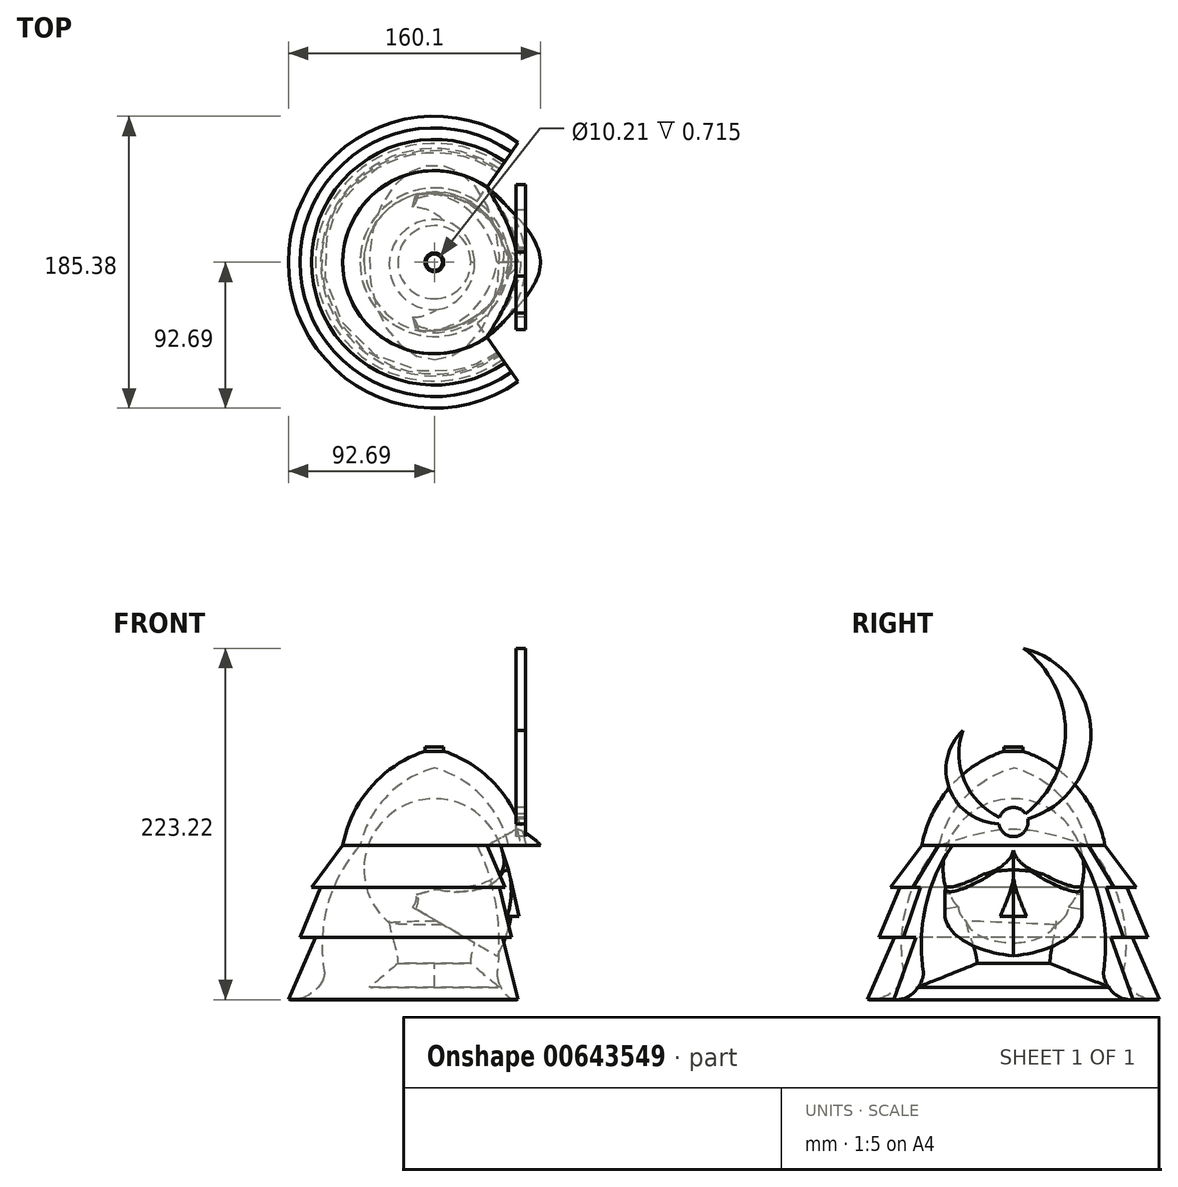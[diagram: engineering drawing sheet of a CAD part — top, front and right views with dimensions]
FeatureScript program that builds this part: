
annotation { "Feature Type Name" : "Feature", "Feature Type Description" : "" }
export const myFeature = defineFeature(function(context is Context, id is Id, definition is map)
    precondition{}
    {
        {
            var Q0;
            Q0=qCreatedBy(makeId("Top.planeOp"),FACE);
            var sketch = newSketch(context, id + "F0", { "sketchPlane" : qUnion([Q0])});
            skArc(sketch, "E0", {"start": v(-44.68, 0) * mm, "mid": v(0, -44.68) * mm, "end": v(44.68, 0) * mm});
            skLineSegment(sketch, "E1", {"start": v(44.68, 0) * mm, "end": v(-44.68, 0) * mm});
            skLineSegment(sketch, "E2", {"start": v(44.68, 0) * mm, "end": v(44.68, 36.03) * mm, "construction": true});
            skSolve(sketch);
        }
        {
            var Q0;
            Q0=qSketchRegion(id+"F0",true);
            var Q1;
            Q1=sQuery(id+"F0.wireOp",EDGE,"E1");
            revolve(context, id + "F1", {"entities" : qUnion([Q0]), "axis" : qUnion([Q1]), "revolveType" : RevolveType.FULL});
        }
        {
            var Q0;
            Q0=makeQuery(id+"F1.opRevolve","SWEPT_BODY",BODY,{"disambiguationData":[OSD([sQuery(id+"F0.wireOp",EDGE,"E0"),sQuery(id+"F0.wireOp",EDGE,"E1")])]});
            var Q1;
            Q1=qCreatedBy(makeId("Top.planeOp"),FACE);
            transform(context, id + "F2", {"entities" : qUnion([Q0]), "transformType" : TransformType.TRANSLATION_DISTANCE, "transformDirection" : qUnion([Q1]), "distance" : 15 * mm, "oppositeDirection" : true, "makeCopy" : false});
        }
        {
            var Q0;
            Q0=qCreatedBy(makeId("Top.planeOp"),FACE);
            var sketch = newSketch(context, id + "F3", { "sketchPlane" : qUnion([Q0])});
            skLineSegment(sketch, "E3", {"start": v(0, 0) * mm, "end": v(12.34, -43.08) * mm});
            skArc(sketch, "E4", {"start": v(12.34, -43.08) * mm, "mid": v(50.67, -33.3) * mm, "end": v(72.02, 0) * mm});
            skLineSegment(sketch, "E5.MirrorCS", {"start": v(0, 0) * mm, "end": v(12.34, 43.08) * mm});
            skLineSegment(sketch, "E6.MirrorCS", {"start": v(12.34, 43.08) * mm, "end": v(12.34, 43.08) * mm});
            skArc(sketch, "E7.MirrorCS", {"start": v(12.34, 43.08) * mm, "mid": v(50.67, 33.3) * mm, "end": v(72.02, 0) * mm});
            skLineSegment(sketch, "E8", {"start": v(0, -61.4) * mm, "end": v(0, 61.38) * mm, "construction": true});
            skPoint(sketch, "E9", {"position": v(42.07, 0) * mm});
            skSolve(sketch);
        }
        {
            var Q0;
            Q0=qSketchRegion(id+"F3",true);
            var Q1;
            Q1=sQuery(id+"F3.wireOp",EDGE,"E8");
            revolve(context, id + "F4", {"entities" : qUnion([Q0]), "axis" : qUnion([Q1]), "revolveType" : RevolveType.ONE_DIRECTION, "angle" : 45 * degree});
        }
        {
            var Q0;
            Q0=makeQuery(id+"F4.opRevolve","SWEPT_BODY",BODY,{"disambiguationData":[OSD([sQuery(id+"F3.wireOp",EDGE,"E3"),sQuery(id+"F3.wireOp",EDGE,"17598f5f-404b-4f8c-ac35-278ca7a2c35a"),sQuery(id+"F3.wireOp",EDGE,"E4"),sQuery(id+"F3.wireOp",EDGE,"5336d24a-33b8-4873-b715-2a8792ee797a"),sQuery(id+"F3.wireOp",EDGE,"E5.MirrorCS"),sQuery(id+"F3.wireOp",EDGE,"E6.MirrorCS"),sQuery(id+"F3.wireOp",EDGE,"E7.MirrorCS"),sQuery(id+"F3.wireOp",EDGE,"d338a3b0-5d36-45a3-872c-7f8dcec3f61b0.MirrorCS")])]});
            var Q1;
            Q1=sQuery(id+"F3.wireOp",EDGE,"E8");
            var Q2;
            Q2=qCreatedBy(makeId("Top.planeOp"),FACE);
            transform(context, id + "F5", {"entities" : qUnion([Q0]), "transformType" : TransformType.TRANSLATION_DISTANCE, "transformDirection" : qUnion([Q2]), "distance" : 15.56 * mm, "oppositeDirection" : true, "makeCopy" : false});
        }
        {
            var Q0;
            Q0=makeQuery(id+"F4.opRevolve","SWEPT_BODY",BODY,{"disambiguationData":[OSD([sQuery(id+"F3.wireOp",EDGE,"E3"),sQuery(id+"F3.wireOp",EDGE,"17598f5f-404b-4f8c-ac35-278ca7a2c35a"),sQuery(id+"F3.wireOp",EDGE,"E4"),sQuery(id+"F3.wireOp",EDGE,"5336d24a-33b8-4873-b715-2a8792ee797a"),sQuery(id+"F3.wireOp",EDGE,"E5.MirrorCS"),sQuery(id+"F3.wireOp",EDGE,"E6.MirrorCS"),sQuery(id+"F3.wireOp",EDGE,"E7.MirrorCS"),sQuery(id+"F3.wireOp",EDGE,"d338a3b0-5d36-45a3-872c-7f8dcec3f61b0.MirrorCS")])]});
            var Q1;
            Q1=qCreatedBy(makeId("Right.planeOp"),FACE);
            transform(context, id + "F6", {"entities" : qUnion([Q0]), "transformType" : TransformType.TRANSLATION_DISTANCE, "transformDirection" : qUnion([Q1]), "distance" : 29.06 * mm, "oppositeDirection" : true, "makeCopy" : false});
        }
        {
            var Q0;
            Q0=makeQuery(id+"F4.opRevolve","SWEPT_BODY",BODY,{"disambiguationData":[OSD([sQuery(id+"F3.wireOp",EDGE,"E3"),sQuery(id+"F3.wireOp",EDGE,"E4"),sQuery(id+"F3.wireOp",EDGE,"E5.MirrorCS"),sQuery(id+"F3.wireOp",EDGE,"E7.MirrorCS")])]});
            var Q1;
            Q1=sQuery(id+"F0.wireOp",EDGE,"E2");
            transform(context, id + "F7", {"entities" : qUnion([Q0]), "transformType" : TransformType.ROTATION, "transformAxis" : qUnion([Q1]), "angle" : 15 * degree, "oppositeDirection" : true, "makeCopy" : false});
        }
        {
            var Q0;
            Q0=makeQuery(id+"F1.opRevolve","SWEPT_BODY",BODY,{"disambiguationData":[OSD([sQuery(id+"F0.wireOp",EDGE,"E0"),sQuery(id+"F0.wireOp",EDGE,"E1")])]});
            var Q1;
            Q1=makeQuery(id+"F4.opRevolve","SWEPT_BODY",BODY,{"disambiguationData":[OSD([sQuery(id+"F3.wireOp",EDGE,"E3"),sQuery(id+"F3.wireOp",EDGE,"17598f5f-404b-4f8c-ac35-278ca7a2c35a"),sQuery(id+"F3.wireOp",EDGE,"E4"),sQuery(id+"F3.wireOp",EDGE,"5336d24a-33b8-4873-b715-2a8792ee797a"),sQuery(id+"F3.wireOp",EDGE,"E5.MirrorCS"),sQuery(id+"F3.wireOp",EDGE,"E6.MirrorCS"),sQuery(id+"F3.wireOp",EDGE,"E7.MirrorCS"),sQuery(id+"F3.wireOp",EDGE,"d338a3b0-5d36-45a3-872c-7f8dcec3f61b0.MirrorCS")])]});
            booleanBodies(context, id + "F8", {"operationType" : BooleanOperationType.UNION, "tools" : qUnion([Q0, Q1])});
        }
        {
            var Q0;
            Q0=qCreatedBy(makeId("Front.planeOp"),FACE);
            var sketch = newSketch(context, id + "F9", { "sketchPlane" : qUnion([Q0])});
            skLineSegment(sketch, "E10", {"start": v(-75.5, -58.39) * mm, "end": v(-92.69, -97.86) * mm});
            skLineSegment(sketch, "E11", {"start": v(0, 63.89) * mm, "end": v(0, -69.8) * mm, "construction": true});
            skLineSegment(sketch, "E12", {"start": v(-72.2, -26.73) * mm, "end": v(-85.33, -58.39) * mm});
            skLineSegment(sketch, "E13", {"start": v(-85.33, -58.39) * mm, "end": v(-75.5, -58.39) * mm});
            skLineSegment(sketch, "E14", {"start": v(-58.16, 0) * mm, "end": v(-78.04, -26.73) * mm});
            skLineSegment(sketch, "E15", {"start": v(-78.04, -26.73) * mm, "end": v(-72.2, -26.73) * mm});
            skLineSegment(sketch, "E16", {"start": v(-47.17, 0) * mm, "end": v(-58.16, 0) * mm});
            skArc(sketch, "E17", {"start": v(-47.17, 0) * mm, "mid": v(-67.66, -37.09) * mm, "end": v(-69.99, -79.4) * mm});
            skArc(sketch, "E18", {"start": v(-92.69, -97.86) * mm, "mid": v(-79.74, -95.06) * mm, "end": v(-70.78, -85.3) * mm});
            skPoint(sketch, "E19.visualSharp", {"position": v(-69.53, -81.9) * mm});
            skArc(sketch, "E19.filletArc", {"start": v(-70.78, -85.3) * mm, "mid": v(-69.93, -82.4) * mm, "end": v(-69.99, -79.4) * mm});
            skSolve(sketch);
        }
        {
            var Q0;
            {var subQ6=sQuery(id+"F9.wireOp",EDGE,"bed17606-2d73-4af0-a236-4f785531fa8f");Q0=makeQuery(id+"F9.imprint","IMPRINT",FACE,{"disambiguationData":[TD([[makeQuery(id+"F9.imprint","IMPRINT",EDGE,{"derivedFrom":subQ6}),1.0]])]});}
            var Q1;
            {var subQ3=sQuery(id+"F9.wireOp",EDGE,"3992ad86-beb6-407e-abb3-2c1991481c55");Q1=makeQuery(id+"F9.imprint","IMPRINT",FACE,{"disambiguationData":[TD([[makeQuery(id+"F9.imprint","IMPRINT",EDGE,{"derivedFrom":subQ3}),1.0]])]});}
            var Q2;
            {var subQ3=sQuery(id+"F9.wireOp",EDGE,"4294b020-6c44-4885-9173-856c7b450247");Q2=makeQuery(id+"F9.imprint","IMPRINT",FACE,{"disambiguationData":[TD([[makeQuery(id+"F9.imprint","IMPRINT",EDGE,{"derivedFrom":subQ3}),1.0]])]});}
            var Q3;
            {var subQ7=sQuery(id+"F9.wireOp",EDGE,"4294b020-6c44-4885-9173-856c7b450247");Q3=makeQuery(id+"F9.imprint","IMPRINT",FACE,{"disambiguationData":[TD([[makeQuery(id+"F9.imprint","IMPRINT",EDGE,{"derivedFrom":subQ7}),-1.0]])]});}
            var Q4;
            {var subQ2=sQuery(id+"F9.wireOp",EDGE,"3992ad86-beb6-407e-abb3-2c1991481c55");Q4=makeQuery(id+"F9.imprint","IMPRINT",FACE,{"disambiguationData":[TD([[makeQuery(id+"F9.imprint","IMPRINT",EDGE,{"derivedFrom":subQ2}),-1.0]])]});}
            var Q5;
            {var subQ0=sQuery(id+"F9.wireOp",EDGE,"E13");var subQ3=sQuery(id+"F9.wireOp",EDGE,"E12");var subQ4=makeQuery(id+"F9.imprint","INTERSECT",VERTEX,{"derivedFrom":[subQ3,subQ0]});Q5=makeQuery(id+"F9.imprint","IMPRINT",FACE,{"disambiguationData":[TD([[makeQuery(id+"F9.imprint","IMPRINT",EDGE,{"disambiguationData":[TD([[subQ4,-1.0]])],"derivedFrom":subQ0}),1.0]])]});}
            var Q6;
            {var subQ0=sQuery(id+"F9.wireOp",EDGE,"E15");var subQ3=sQuery(id+"F9.wireOp",EDGE,"E14");var subQ4=makeQuery(id+"F9.imprint","INTERSECT",VERTEX,{"derivedFrom":[subQ3,subQ0]});Q6=makeQuery(id+"F9.imprint","IMPRINT",FACE,{"disambiguationData":[TD([[makeQuery(id+"F9.imprint","IMPRINT",EDGE,{"disambiguationData":[TD([[subQ4,-1.0]])],"derivedFrom":subQ0}),1.0]])]});}
            var Q7;
            Q7=sQuery(id+"F9.wireOp",EDGE,"E11");
            revolve(context, id + "F10", {"entities" : qUnion([Q0, Q1, Q2, Q3, Q4, Q5, Q6]), "axis" : qUnion([Q7]), "revolveType" : RevolveType.SYMMETRIC, "angle" : 250 * degree});
        }
        {
            var Q0;
            Q0=qCreatedBy(makeId("Right.planeOp"),FACE);
            var sketch = newSketch(context, id + "F11", { "sketchPlane" : qUnion([Q0])});
            skArc(sketch, "E20", {"start": v(0, 61.56) * mm, "mid": v(-38.19, 39.4) * mm, "end": v(-58.14, 0) * mm});
            skArc(sketch, "E21", {"start": v(0, 49.28) * mm, "mid": v(-30.36, 31.11) * mm, "end": v(-47.2, 0) * mm});
            skLineSegment(sketch, "E22", {"start": v(0, 61.56) * mm, "end": v(0, 49.28) * mm});
            skLineSegment(sketch, "E23", {"start": v(-58.14, 0) * mm, "end": v(-47.2, 0) * mm});
            skSolve(sketch);
        }
        {
            var Q0;
            Q0=makeQuery(id+"F11.imprint","IMPRINT",FACE,{"disambiguationData":[TD([[makeQuery(id+"F11.imprint","IMPRINT",EDGE,{"derivedFrom":sQuery(id+"F11.wireOp",EDGE,"E20")}),1.0]])]});
            var Q1;
            Q1=sQuery(id+"F11.wireOp",EDGE,"E22");
            revolve(context, id + "F12", {"entities" : qUnion([Q0]), "axis" : qUnion([Q1]), "revolveType" : RevolveType.FULL});
        }
        {
            var Q0;
            Q0=qCreatedBy(makeId("Right.planeOp"),FACE);
            var sketch = newSketch(context, id + "F13", { "sketchPlane" : qUnion([Q0])});
            skArc(sketch, "E24", {"start": v(-32.22, 58.1) * mm, "mid": v(-38.56, 16.6) * mm, "end": v(0, 0) * mm});
            skArc(sketch, "E25", {"start": v(-32.22, 58.1) * mm, "mid": v(-29.07, 21.86) * mm, "end": v(0, 0) * mm});
            skCircle(sketch, "E26", {"center": v(0, 0) * mm, "radius": 9.26 * mm});
            skArc(sketch, "E27", {"start": v(0, 0) * mm, "mid": v(49.07, 52.54) * mm, "end": v(6.38, 110.39) * mm});
            skArc(sketch, "E28", {"start": v(0, 0) * mm, "mid": v(32.95, 53.47) * mm, "end": v(6.38, 110.39) * mm});
            skSolve(sketch);
        }
        {
            var Q0;
            Q0=qSketchRegion(id+"F13",true);
            extrude(context, id + "F14", {"entities" : qUnion([Q0]), "depth" : 6 * mm});
        }
        {
            var Q0;
            Q0=makeQuery(id+"F14.opExtrude","SWEPT_BODY",BODY,{"disambiguationData":[OSD([sQuery(id+"F13.wireOp",EDGE,"63a4e0e8-54da-4c7c-8e49-798323a95d9c0.MirrorCS"),sQuery(id+"F13.wireOp",EDGE,"63a4e0e8-54da-4c7c-8e49-798323a95d9c1.MirrorCS"),sQuery(id+"F13.wireOp",EDGE,"63a4e0e8-54da-4c7c-8e49-798323a95d9c2.MirrorCS"),sQuery(id+"F13.wireOp",EDGE,"63a4e0e8-54da-4c7c-8e49-798323a95d9c3.MirrorCS"),sQuery(id+"F13.wireOp",EDGE,"63a4e0e8-54da-4c7c-8e49-798323a95d9c4.MirrorCS"),sQuery(id+"F13.wireOp",EDGE,"63a4e0e8-54da-4c7c-8e49-798323a95d9c5.MirrorCS")])]});
            var Q1;
            Q1=makeQuery(id+"F14.opExtrude","SWEPT_BODY",BODY,{"disambiguationData":[OSD([sQuery(id+"F13.wireOp",EDGE,"E24"),sQuery(id+"F13.wireOp",EDGE,"b7e1e591-e3d9-4fc4-9fd9-ac906eb5375b"),sQuery(id+"F13.wireOp",EDGE,"b3045065-7fd3-4527-97a0-abc5098df0ba"),sQuery(id+"F13.wireOp",EDGE,"015c9c46-c47a-4591-99de-78b190910ab0"),sQuery(id+"F13.wireOp",EDGE,"8cbf14fa-2419-4e41-a801-432650f1cecd"),sQuery(id+"F13.wireOp",EDGE,"E25")])]});
            var Q2;
            Q2=qCreatedBy(makeId("Right.planeOp"),FACE);
            transform(context, id + "F15", {"entities" : qUnion([Q0, Q1]), "transformType" : TransformType.TRANSLATION_DISTANCE, "transformDirection" : qUnion([Q2]), "distance" : 51.95 * mm, "makeCopy" : false});
        }
        {
            var Q0;
            Q0=qCreatedBy(makeId("Front.planeOp"),FACE);
            var sketch = newSketch(context, id + "F16", { "sketchPlane" : qUnion([Q0])});
            skLineSegment(sketch, "E29.bottom", {"start": v(0, 62.6) * mm, "end": v(-5.96, 62.6) * mm});
            skLineSegment(sketch, "E29.top", {"start": v(0, 58.52) * mm, "end": v(-5.96, 58.52) * mm});
            skLineSegment(sketch, "E29.left", {"start": v(0, 62.6) * mm, "end": v(0, 58.52) * mm});
            skLineSegment(sketch, "E29.right", {"start": v(-5.96, 62.6) * mm, "end": v(-5.96, 58.52) * mm});
            skLineSegment(sketch, "E30.bottom", {"start": v(-5.1, 62.9) * mm, "end": v(1.24, 62.9) * mm});
            skLineSegment(sketch, "E30.top", {"start": v(-5.1, 61.9) * mm, "end": v(1.24, 61.9) * mm});
            skLineSegment(sketch, "E30.left", {"start": v(-5.1, 62.9) * mm, "end": v(-5.1, 61.9) * mm});
            skLineSegment(sketch, "E30.right", {"start": v(1.24, 62.9) * mm, "end": v(1.24, 61.9) * mm});
            skSolve(sketch);
        }
        {
            var Q0;
            {var subQ8=sQuery(id+"F16.wireOp",EDGE,"E29.top");Q0=makeQuery(id+"F16.imprint","IMPRINT",FACE,{"disambiguationData":[TD([[makeQuery(id+"F16.imprint","IMPRINT",EDGE,{"derivedFrom":subQ8}),-1.0]])]});}
            var Q1;
            Q1=sQuery(id+"F11.wireOp",EDGE,"E22");
            revolve(context, id + "F17", {"operationType" : NewBodyOperationType.ADD, "entities" : qUnion([Q0]), "axis" : qUnion([Q1]), "revolveType" : RevolveType.FULL});
        }
        {
            var Q0;
            Q0=makeQuery(id+"F14.opExtrude","SWEPT_BODY",BODY,{"disambiguationData":[OSD([sQuery(id+"F13.wireOp",EDGE,"E24"),sQuery(id+"F13.wireOp",EDGE,"b7e1e591-e3d9-4fc4-9fd9-ac906eb5375b"),sQuery(id+"F13.wireOp",EDGE,"b3045065-7fd3-4527-97a0-abc5098df0ba"),sQuery(id+"F13.wireOp",EDGE,"015c9c46-c47a-4591-99de-78b190910ab0"),sQuery(id+"F13.wireOp",EDGE,"8cbf14fa-2419-4e41-a801-432650f1cecd"),sQuery(id+"F13.wireOp",EDGE,"E25"),sQuery(id+"F13.wireOp",EDGE,"63a4e0e8-54da-4c7c-8e49-798323a95d9c0.MirrorCS"),sQuery(id+"F13.wireOp",EDGE,"63a4e0e8-54da-4c7c-8e49-798323a95d9c1.MirrorCS"),sQuery(id+"F13.wireOp",EDGE,"63a4e0e8-54da-4c7c-8e49-798323a95d9c2.MirrorCS"),sQuery(id+"F13.wireOp",EDGE,"63a4e0e8-54da-4c7c-8e49-798323a95d9c3.MirrorCS"),sQuery(id+"F13.wireOp",EDGE,"63a4e0e8-54da-4c7c-8e49-798323a95d9c4.MirrorCS"),sQuery(id+"F13.wireOp",EDGE,"63a4e0e8-54da-4c7c-8e49-798323a95d9c5.MirrorCS"),sQuery(id+"F13.wireOp",EDGE,"E26")])]});
            var Q1;
            Q1=qCreatedBy(makeId("Top.planeOp"),FACE);
            transform(context, id + "F18", {"entities" : qUnion([Q0]), "transformType" : TransformType.TRANSLATION_DISTANCE, "transformDirection" : qUnion([Q1]), "distance" : 14.88 * mm, "makeCopy" : false});
        }
        {
            var Q0;
            Q0=qCreatedBy(makeId("Front.planeOp"),FACE);
            var sketch = newSketch(context, id + "F19", { "sketchPlane" : qUnion([Q0])});
            skLineSegment(sketch, "E31", {"start": v(67.4, 0.05) * mm, "end": v(55, 0.05) * mm});
            skLineSegment(sketch, "E32", {"start": v(55, 0.05) * mm, "end": v(52.48, 10.4) * mm});
            skArc(sketch, "E33", {"start": v(67.4, 0.05) * mm, "mid": v(60.62, 6.2) * mm, "end": v(52.48, 10.4) * mm});
            skSolve(sketch);
        }
        {
            var Q0;
            Q0=makeQuery(id+"F10.opRevolve","CAP_VERTEX",VERTEX,{"disambiguationData":[OSD([sQuery(id+"F9.wireOp",EDGE,"E14"),sQuery(id+"F9.wireOp",EDGE,"E16")])],"isStart":true});
            var Q1;
            Q1=makeQuery(id+"F19.imprint","IMPRINT",FACE,{"disambiguationData":[TD([[makeQuery(id+"F19.imprint","IMPRINT",EDGE,{"derivedFrom":sQuery(id+"F19.wireOp",EDGE,"E31")}),-1.0]])]});
            var Q2;
            Q2=makeQuery(id+"F10.opRevolve","CAP_VERTEX",VERTEX,{"disambiguationData":[OSD([sQuery(id+"F9.wireOp",EDGE,"E14"),sQuery(id+"F9.wireOp",EDGE,"E16")])],"isStart":false});
            loft(context, id + "F20", {"sheetProfilesArray" : [{ "sheetProfileEntities" : qUnion([Q0]) }, { "sheetProfileEntities" : qUnion([Q1]) }, { "sheetProfileEntities" : qUnion([Q2]) }]});
        }
        {
            var Q0;
            Q0=qCreatedBy(makeId("Top.planeOp"),FACE);
            cPlane(context, id + "F21", {"entities" : qUnion([Q0]), "cplaneType" : CPlaneType.OFFSET, "offset" : 90 * mm, "oppositeDirection" : true, "width" : 150 * mm, "height" : 150 * mm});
        }
        {
            var Q0;
            Q0=qCreatedBy(id+"F21.planeOp",FACE);
            var sketch = newSketch(context, id + "F22", { "sketchPlane" : qUnion([Q0])});
            skEllipse(sketch, "E34", {"center": v(0, 0) * mm, "majorRadius": 61.75 * mm, "minorRadius": 41.4 * mm, "majorAxis": v(0, -1)});
            skSolve(sketch);
        }
        {
            var Q0;
            Q0=qCreatedBy(id+"F21.planeOp",FACE);
            cPlane(context, id + "F23", {"entities" : qUnion([Q0]), "cplaneType" : CPlaneType.OFFSET, "offset" : 15 * mm, "width" : 150 * mm, "height" : 150 * mm});
        }
        {
            var Q0;
            Q0=qCreatedBy(id+"F23.planeOp",FACE);
            var sketch = newSketch(context, id + "F24", { "sketchPlane" : qUnion([Q0])});
            skCircle(sketch, "E35", {"center": v(0, 0) * mm, "radius": 23.2 * mm});
            skSolve(sketch);
        }
        {
            var Q0;
            Q0=qCreatedBy(id+"F23.planeOp",FACE);
            cPlane(context, id + "F25", {"entities" : qUnion([Q0]), "cplaneType" : CPlaneType.OFFSET, "offset" : 30 * mm, "width" : 150 * mm, "height" : 150 * mm});
        }
        {
            var Q0;
            Q0=qCreatedBy(id+"F25.planeOp",FACE);
            var sketch = newSketch(context, id + "F26", { "sketchPlane" : qUnion([Q0])});
            skCircle(sketch, "E36", {"center": v(0, -1.42) * mm, "radius": 28.98 * mm});
            skArc(sketch, "E37", {"start": v(33.36, -9.72) * mm, "mid": v(45.44, -8.86) * mm, "end": v(53.7, 0) * mm});
            skArc(sketch, "E38.MirrorCS", {"start": v(33.36, 9.72) * mm, "mid": v(45.44, 8.86) * mm, "end": v(53.7, 0) * mm});
            skLineSegment(sketch, "E39", {"start": v(33.36, -9.72) * mm, "end": v(33.36, 9.72) * mm});
            skSolve(sketch);
        }
        {
            var Q1;
            {var subQ0=sQuery(id+"F3.wireOp",EDGE,"E4");var subQ1=sQuery(id+"F3.wireOp",EDGE,"E7.MirrorCS");Q1=makeQuery(id+"F8.opBoolean","SPLIT",FACE,{"disambiguationData":[TD([makeQuery(id+"F1.opRevolve","SWEPT_FACE",FACE,{"disambiguationData":[OSD([sQuery(id+"F0.wireOp",EDGE,"E0")])]}),makeQuery(id+"F4.opRevolve","SWEPT_FACE",FACE,{"disambiguationData":[OSD([subQ0])]}),makeQuery(id+"F4.opRevolve","SWEPT_FACE",FACE,{"disambiguationData":[OSD([subQ1])]})])],"derivedFrom":makeQuery(id+"F4.opRevolve","CAP_FACE",FACE,{"disambiguationData":[OSD([sQuery(id+"F3.wireOp",EDGE,"E3"),subQ0,sQuery(id+"F3.wireOp",EDGE,"E5.MirrorCS"),subQ1])],"isStart":true})});}
            var Q2;
            Q2=sQuery(id+"F3.wireOp",VERTEX,"E9");
            loft(context, id + "F27", {"operationType" : NewBodyOperationType.ADD, "sheetProfilesArray" : [{ "sheetProfileEntities" : qUnion([Q1]) }, { "sheetProfileEntities" : qUnion([Q2]) }]});
        }
        {
            var Q0;
            Q0=makeQuery(id+"F8.opBoolean","INTERSECT",EDGE,{"derivedFrom":[makeQuery(id+"F1.opRevolve","SWEPT_FACE",FACE,{"disambiguationData":[OSD([sQuery(id+"F0.wireOp",EDGE,"E0")])]}),makeQuery(id+"F4.opRevolve","SWEPT_FACE",FACE,{"disambiguationData":[OSD([sQuery(id+"F3.wireOp",EDGE,"E7.MirrorCS")])]})]});
            var Q1;
            Q1=makeQuery(id+"F8.opBoolean","INTERSECT",EDGE,{"derivedFrom":[makeQuery(id+"F1.opRevolve","SWEPT_FACE",FACE,{"disambiguationData":[OSD([sQuery(id+"F0.wireOp",EDGE,"E0")])]}),makeQuery(id+"F4.opRevolve","SWEPT_FACE",FACE,{"disambiguationData":[OSD([sQuery(id+"F3.wireOp",EDGE,"E4")])]})]});
            fillet(context, id + "F28", {"entities" : qUnion([Q0, Q1]), "radius" : 10 * mm, "tangentPropagation" : true, "allowEdgeOverflow" : false});
        }
        {
            var Q1;
            Q1=makeQuery(id+"F26.imprint","IMPRINT",FACE,{"disambiguationData":[TD([[makeQuery(id+"F26.imprint","IMPRINT",EDGE,{"derivedFrom":sQuery(id+"F26.wireOp",EDGE,"E37")}),1.0]])]});
            var Q2;
            {var subQ0=sQuery(id+"F3.wireOp",EDGE,"E4");var subQ1=sQuery(id+"F3.wireOp",EDGE,"E7.MirrorCS");Q2=makeQuery(id+"F27.boolean.opBoolean","MERGE",VERTEX,{"derivedFrom":[makeQuery(id+"F4.opRevolve","CAP_VERTEX",VERTEX,{"disambiguationData":[OSD([subQ0,subQ1])],"isStart":true}),makeQuery(id+"F27.opLoft","MID_CAP_VERTEX",VERTEX,{"disambiguationData":[OSD([subQ0,subQ1])],"capPos":0.0})]});}
            loft(context, id + "F29", {"operationType" : NewBodyOperationType.ADD, "sheetProfilesArray" : [{ "sheetProfileEntities" : qUnion([Q1]) }, { "sheetProfileEntities" : qUnion([Q2]) }]});
        }
        {
            var Q0;
            Q0=makeQuery(id+"F22.imprint","IMPRINT",FACE,{"disambiguationData":[TD([[makeQuery(id+"F22.imprint","IMPRINT",EDGE,{"derivedFrom":sQuery(id+"F22.wireOp",EDGE,"E34")}),1.0]])]});
            var Q1;
            Q1=makeQuery(id+"F24.imprint","IMPRINT",FACE,{"disambiguationData":[TD([[makeQuery(id+"F24.imprint","IMPRINT",EDGE,{"derivedFrom":sQuery(id+"F24.wireOp",EDGE,"E35")}),1.0]])]});
            loft(context, id + "F30", {"startCondition" : LoftEndDerivativeType.TANGENT_TO_PROFILE, "startMagnitude" : 0.1, "sheetProfilesArray" : [{ "sheetProfileEntities" : qUnion([Q0]) }, { "sheetProfileEntities" : qUnion([Q1]) }]});
        }
        {
            var Q1;
            Q1=makeQuery(id+"F24.imprint","IMPRINT",FACE,{"disambiguationData":[TD([[makeQuery(id+"F24.imprint","IMPRINT",EDGE,{"derivedFrom":sQuery(id+"F24.wireOp",EDGE,"E35")}),1.0]])]});
            var Q2;
            Q2=makeQuery(id+"F26.imprint","IMPRINT",FACE,{"disambiguationData":[TD([[makeQuery(id+"F26.imprint","IMPRINT",EDGE,{"derivedFrom":sQuery(id+"F26.wireOp",EDGE,"E36")}),1.0]])]});
            loft(context, id + "F31", {"operationType" : NewBodyOperationType.ADD, "startCondition" : LoftEndDerivativeType.NORMAL_TO_PROFILE, "startMagnitude" : 1, "endCondition" : LoftEndDerivativeType.NORMAL_TO_PROFILE, "endMagnitude" : 1, "sheetProfilesArray" : [{ "sheetProfileEntities" : qUnion([Q1]) }, { "sheetProfileEntities" : qUnion([Q2]) }]});
        }
    });
